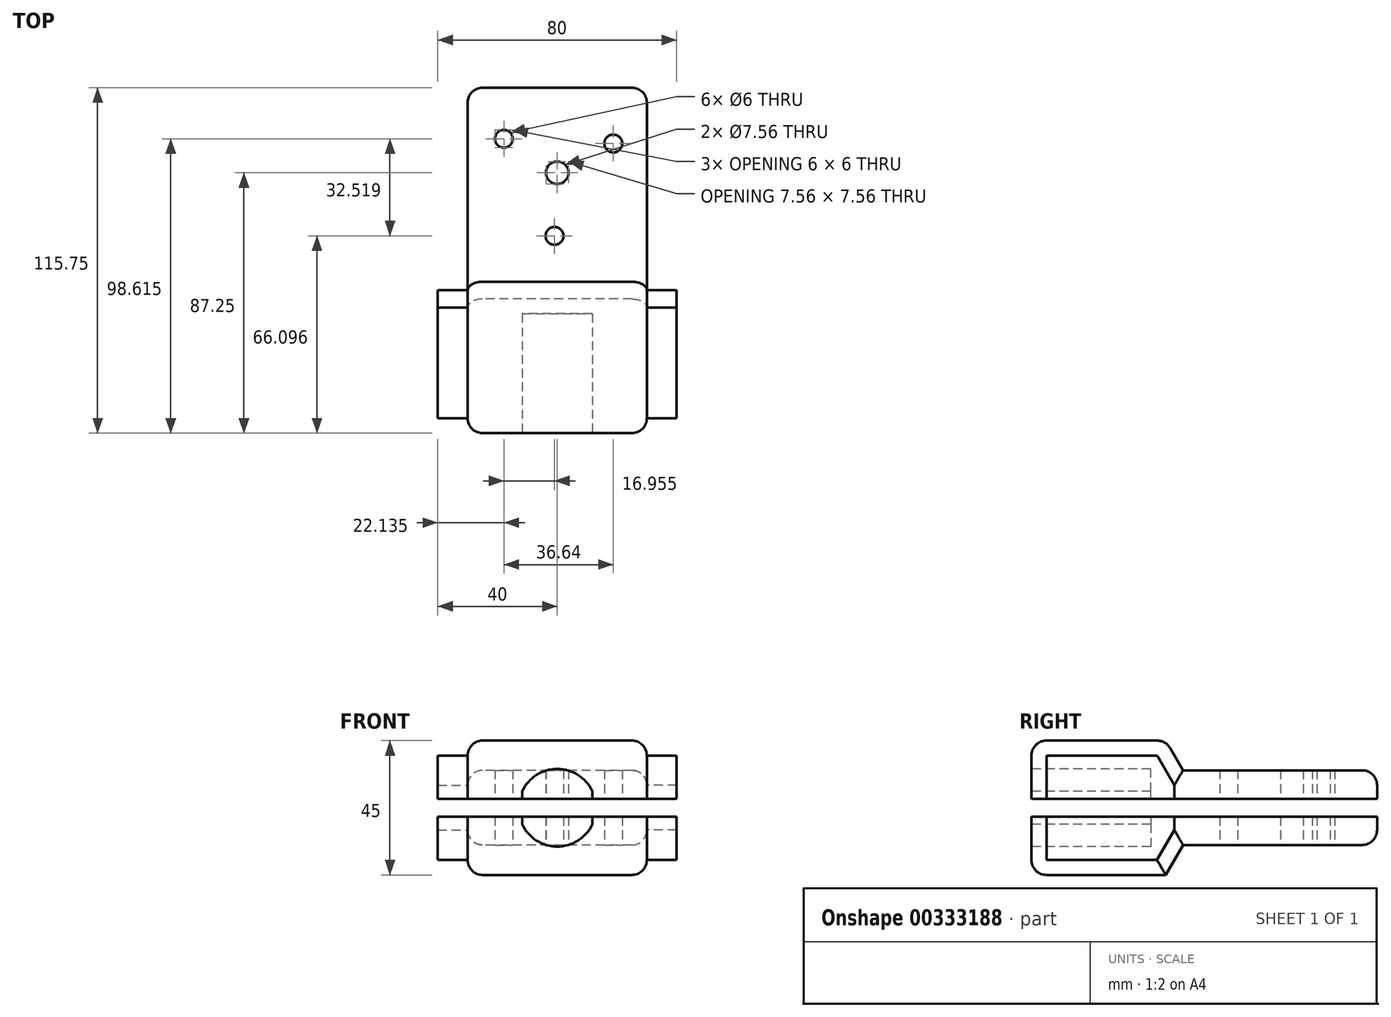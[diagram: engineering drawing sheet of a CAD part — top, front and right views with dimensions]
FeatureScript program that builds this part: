
annotation { "Feature Type Name" : "Feature", "Feature Type Description" : "" }
export const myFeature = defineFeature(function(context is Context, id is Id, definition is map)
    precondition{}
    {
        {
            var Q0;
            Q0=qCreatedBy(makeId("Right.planeOp"),FACE);
            var sketch = newSketch(context, id + "F0", { "sketchPlane" : qUnion([Q0])});
            skLineSegment(sketch, "E0", {"start": v(-50.75, 9.96) * mm, "end": v(-5.75, 9.96) * mm});
            skLineSegment(sketch, "E1", {"start": v(65, 0) * mm, "end": v(65, -25) * mm});
            skLineSegment(sketch, "E2", {"start": v(65, -25) * mm, "end": v(0, -25) * mm});
            skLineSegment(sketch, "E3", {"start": v(0, -25) * mm, "end": v(-5.8, -35.04) * mm});
            skLineSegment(sketch, "E4", {"start": v(-5.8, -35.04) * mm, "end": v(-50.75, -35.04) * mm});
            skLineSegment(sketch, "E5", {"start": v(-50.75, -35.04) * mm, "end": v(-50.75, 9.96) * mm});
            skLineSegment(sketch, "E6", {"start": v(0, 0) * mm, "end": v(-5.75, 9.96) * mm});
            skLineSegment(sketch, "E7", {"start": v(0, 0) * mm, "end": v(65, 0) * mm});
            skSolve(sketch);
        }
        {
            var Q0;
            Q0=qSketchRegion(id+"F0",true);
            extrude(context, id + "F1", {"entities" : qUnion([Q0]), "endBound" : BoundingType.SYMMETRIC, "depth" : 60 * mm});
        }
        {
            var Q0;
            Q0=makeQuery(id+"F1.opExtrude","SWEPT_FACE",FACE,{"disambiguationData":[OSD([sQuery(id+"F0.wireOp",EDGE,"E5")])]});
            var sketch = newSketch(context, id + "F2", { "sketchPlane" : qUnion([Q0])});
            skLineSegment(sketch, "E8", {"start": v(0, -35.04) * mm, "end": v(0, 9.96) * mm, "construction": true});
            skCircle(sketch, "E9", {"center": v(0, -12.54) * mm, "radius": 13 * mm});
            skSolve(sketch);
        }
        {
            var Q0;
            Q0=qSketchRegion(id+"F2",true);
            extrude(context, id + "F3", {"entities" : qUnion([Q0]), "operationType" : NewBodyOperationType.REMOVE, "oppositeDirection" : true, "depth" : 40 * mm});
        }
        {
            var Q0;
            Q0=makeQuery(id+"F1.opExtrude","SWEPT_EDGE",EDGE,{"disambiguationData":[OSD([sQuery(id+"F0.wireOp",EDGE,"E1"),sQuery(id+"F0.wireOp",EDGE,"E7")])]});
            var Q1;
            Q1=makeQuery(id+"F1.opExtrude","SWEPT_EDGE",EDGE,{"disambiguationData":[OSD([sQuery(id+"F0.wireOp",EDGE,"E1"),sQuery(id+"F0.wireOp",EDGE,"E2")])]});
            var Q2;
            Q2=makeQuery(id+"F1.opExtrude","CAP_EDGE",EDGE,{"disambiguationData":[OSD([sQuery(id+"F0.wireOp",EDGE,"E1")])],"isStart":true});
            var Q3;
            Q3=makeQuery(id+"F1.opExtrude","CAP_EDGE",EDGE,{"disambiguationData":[OSD([sQuery(id+"F0.wireOp",EDGE,"E1")])],"isStart":false});
            var Q4;
            Q4=makeQuery(id+"F1.opExtrude","CAP_EDGE",EDGE,{"disambiguationData":[OSD([sQuery(id+"F0.wireOp",EDGE,"E7")])],"isStart":false});
            var Q5;
            Q5=makeQuery(id+"F1.opExtrude","CAP_EDGE",EDGE,{"disambiguationData":[OSD([sQuery(id+"F0.wireOp",EDGE,"E2")])],"isStart":false});
            var Q6;
            Q6=makeQuery(id+"F1.opExtrude","CAP_EDGE",EDGE,{"disambiguationData":[OSD([sQuery(id+"F0.wireOp",EDGE,"E2")])],"isStart":true});
            var Q7;
            Q7=makeQuery(id+"F1.opExtrude","CAP_EDGE",EDGE,{"disambiguationData":[OSD([sQuery(id+"F0.wireOp",EDGE,"E7")])],"isStart":true});
            var Q8;
            Q8=makeQuery(id+"F1.opExtrude","SWEPT_EDGE",EDGE,{"disambiguationData":[OSD([sQuery(id+"F0.wireOp",EDGE,"E0"),sQuery(id+"F0.wireOp",EDGE,"E6")])]});
            var Q9;
            Q9=makeQuery(id+"F1.opExtrude","CAP_EDGE",EDGE,{"disambiguationData":[OSD([sQuery(id+"F0.wireOp",EDGE,"E0")])],"isStart":false});
            var Q10;
            Q10=makeQuery(id+"F1.opExtrude","SWEPT_EDGE",EDGE,{"disambiguationData":[OSD([sQuery(id+"F0.wireOp",EDGE,"E0"),sQuery(id+"F0.wireOp",EDGE,"E5")])]});
            var Q11;
            Q11=makeQuery(id+"F1.opExtrude","CAP_EDGE",EDGE,{"disambiguationData":[OSD([sQuery(id+"F0.wireOp",EDGE,"E0")])],"isStart":true});
            var Q12;
            Q12=makeQuery(id+"F1.opExtrude","CAP_EDGE",EDGE,{"disambiguationData":[OSD([sQuery(id+"F0.wireOp",EDGE,"E6")])],"isStart":false});
            var Q13;
            Q13=makeQuery(id+"F1.opExtrude","CAP_EDGE",EDGE,{"disambiguationData":[OSD([sQuery(id+"F0.wireOp",EDGE,"E6")])],"isStart":true});
            var Q14;
            Q14=makeQuery(id+"F1.opExtrude","CAP_EDGE",EDGE,{"disambiguationData":[OSD([sQuery(id+"F0.wireOp",EDGE,"E3")])],"isStart":false});
            var Q15;
            Q15=makeQuery(id+"F1.opExtrude","CAP_EDGE",EDGE,{"disambiguationData":[OSD([sQuery(id+"F0.wireOp",EDGE,"E3")])],"isStart":true});
            var Q16;
            Q16=makeQuery(id+"F1.opExtrude","CAP_EDGE",EDGE,{"disambiguationData":[OSD([sQuery(id+"F0.wireOp",EDGE,"E4")])],"isStart":false});
            var Q17;
            Q17=makeQuery(id+"F1.opExtrude","CAP_EDGE",EDGE,{"disambiguationData":[OSD([sQuery(id+"F0.wireOp",EDGE,"E4")])],"isStart":true});
            var Q18;
            Q18=makeQuery(id+"F1.opExtrude","SWEPT_EDGE",EDGE,{"disambiguationData":[OSD([sQuery(id+"F0.wireOp",EDGE,"E4"),sQuery(id+"F0.wireOp",EDGE,"E5")])]});
            var Q19;
            Q19=makeQuery(id+"F1.opExtrude","CAP_EDGE",EDGE,{"disambiguationData":[OSD([sQuery(id+"F0.wireOp",EDGE,"E5")])],"isStart":false});
            var Q20;
            Q20=makeQuery(id+"F1.opExtrude","CAP_EDGE",EDGE,{"disambiguationData":[OSD([sQuery(id+"F0.wireOp",EDGE,"E5")])],"isStart":true});
            fillet(context, id + "F4", {"entities" : qUnion([Q0, Q1, Q2, Q3, Q4, Q5, Q6, Q7, Q8, Q9, Q10, Q11, Q12, Q13, Q14, Q15, Q16, Q17, Q18, Q19, Q20]), "radius" : 5 * mm, "tangentPropagation" : true, "allowEdgeOverflow" : false});
        }
        {
            var Q0;
            Q0=makeQuery(id+"F1.opExtrude","SWEPT_FACE",FACE,{"disambiguationData":[OSD([sQuery(id+"F0.wireOp",EDGE,"E2")])]});
            var sketch = newSketch(context, id + "F5", { "sketchPlane" : qUnion([Q0])});
            skCircle(sketch, "E10", {"center": v(-17.86, -47.86) * mm, "radius": 3 * mm});
            skCircle(sketch, "E11.1.0", {"center": v(18.77, -46.29) * mm, "radius": 3 * mm});
            skCircle(sketch, "E11.2.0", {"center": v(-0.9, -15.35) * mm, "radius": 3 * mm});
            skPoint(sketch, "E11.center", {"position": v(0, -36.5) * mm});
            skCircle(sketch, "E12", {"center": v(0, -36.5) * mm, "radius": 3.78 * mm});
            skSolve(sketch);
        }
        {
            var Q0;
            Q0=qSketchRegion(id+"F5",true);
            extrude(context, id + "F6", {"entities" : qUnion([Q0]), "operationType" : NewBodyOperationType.REMOVE, "oppositeDirection" : true, "depth" : 39.9 * mm});
        }
        {
            var Q0;
            Q0=makeQuery(id+"F1.opExtrude","SWEPT_FACE",FACE,{"disambiguationData":[OSD([sQuery(id+"F0.wireOp",EDGE,"E5")])]});
            var sketch = newSketch(context, id + "F7", { "sketchPlane" : qUnion([Q0])});
            skLineSegment(sketch, "E13", {"start": v(-25, -7.04) * mm, "end": v(25, -7.04) * mm});
            skLineSegment(sketch, "E14", {"start": v(25, -7.04) * mm, "end": v(25, -18.04) * mm});
            skLineSegment(sketch, "E15", {"start": v(25, -18.04) * mm, "end": v(-25, -18.04) * mm});
            skLineSegment(sketch, "E16", {"start": v(-25, -18.04) * mm, "end": v(-25, -7.04) * mm});
            skLineSegment(sketch, "E17", {"start": v(-25, -7.04) * mm, "end": v(-35.45, -7.04) * mm});
            skLineSegment(sketch, "E18", {"start": v(-35.45, -7.04) * mm, "end": v(-35.45, -18.04) * mm});
            skLineSegment(sketch, "E19", {"start": v(-35.45, -18.04) * mm, "end": v(-25, -18.04) * mm});
            skLineSegment(sketch, "E20", {"start": v(25, -7.04) * mm, "end": v(35.45, -7.04) * mm});
            skLineSegment(sketch, "E21", {"start": v(35.45, -7.04) * mm, "end": v(35.45, -18.04) * mm});
            skLineSegment(sketch, "E22", {"start": v(35.45, -18.04) * mm, "end": v(25, -18.04) * mm});
            skSolve(sketch);
        }
        {
            var Q0;
            Q0=qSketchRegion(id+"F7",true);
            extrude(context, id + "F8", {"entities" : qUnion([Q0]), "operationType" : NewBodyOperationType.REMOVE, "oppositeDirection" : true, "depth" : 159.3 * mm});
        }
        {
            var Q0;
            Q0=makeQuery(id+"F1.opExtrude","CAP_FACE",FACE,{"disambiguationData":[OSD([sQuery(id+"F0.wireOp",EDGE,"E0"),sQuery(id+"F0.wireOp",EDGE,"E1"),sQuery(id+"F0.wireOp",EDGE,"E2"),sQuery(id+"F0.wireOp",EDGE,"E3"),sQuery(id+"F0.wireOp",EDGE,"E4"),sQuery(id+"F0.wireOp",EDGE,"E5"),sQuery(id+"F0.wireOp",EDGE,"E6"),sQuery(id+"F0.wireOp",EDGE,"E7")])],"isStart":false});
            extrude(context, id + "F9", {"entities" : qUnion([Q0]), "operationType" : NewBodyOperationType.ADD, "depth" : 10 * mm});
        }
        {
            var Q0;
            {var subQ0=sQuery(id+"F0.wireOp",EDGE,"E7");var subQ1=sQuery(id+"F0.wireOp",EDGE,"E6");var subQ2=sQuery(id+"F0.wireOp",EDGE,"E5");var subQ3=sQuery(id+"F0.wireOp",EDGE,"E4");var subQ4=sQuery(id+"F0.wireOp",EDGE,"E3");var subQ5=sQuery(id+"F0.wireOp",EDGE,"E2");var subQ6=sQuery(id+"F0.wireOp",EDGE,"E1");var subQ7=sQuery(id+"F0.wireOp",EDGE,"E0");Q0=makeQuery(id+"F9.opExtrude","SWEPT_FACE",FACE,{"disambiguationData":[OSD([subQ7,subQ6,subQ5,subQ4,subQ3,subQ2,subQ1,subQ0]),TDD([makeQuery(id+"F4.opFillet","BLEND_EDGE",EDGE,{"blendedFrom":[makeQuery(id+"F1.opExtrude","CAP_EDGE",EDGE,{"disambiguationData":[OSD([subQ0])],"isStart":false}),makeQuery(id+"F1.opExtrude","CAP_FACE",FACE,{"disambiguationData":[OSD([subQ7,subQ6,subQ5,subQ4,subQ3,subQ2,subQ1,subQ0])],"isStart":false})],"blendedInto":[makeQuery(id+"F1.opExtrude","CAP_FACE",FACE,{"disambiguationData":[OSD([subQ7,subQ6,subQ5,subQ4,subQ3,subQ2,subQ1,subQ0])],"isStart":false})]})])]});}
            extrude(context, id + "F10", {"entities" : qUnion([Q0]), "operationType" : NewBodyOperationType.REMOVE, "oppositeDirection" : true, "depth" : 25 * mm});
        }
        {
            var Q0;
            Q0=makeQuery(id+"F1.opExtrude","CAP_FACE",FACE,{"disambiguationData":[OSD([sQuery(id+"F0.wireOp",EDGE,"E0"),sQuery(id+"F0.wireOp",EDGE,"E1"),sQuery(id+"F0.wireOp",EDGE,"E2"),sQuery(id+"F0.wireOp",EDGE,"E3"),sQuery(id+"F0.wireOp",EDGE,"E4"),sQuery(id+"F0.wireOp",EDGE,"E5"),sQuery(id+"F0.wireOp",EDGE,"E6"),sQuery(id+"F0.wireOp",EDGE,"E7")])],"isStart":true});
            extrude(context, id + "F11", {"entities" : qUnion([Q0]), "operationType" : NewBodyOperationType.ADD, "depth" : 10 * mm});
        }
        {
            var Q0;
            {var subQ0=sQuery(id+"F0.wireOp",EDGE,"E7");var subQ1=sQuery(id+"F0.wireOp",EDGE,"E6");var subQ2=sQuery(id+"F0.wireOp",EDGE,"E5");var subQ3=sQuery(id+"F0.wireOp",EDGE,"E4");var subQ4=sQuery(id+"F0.wireOp",EDGE,"E3");var subQ5=sQuery(id+"F0.wireOp",EDGE,"E2");var subQ6=sQuery(id+"F0.wireOp",EDGE,"E1");var subQ7=sQuery(id+"F0.wireOp",EDGE,"E0");Q0=makeQuery(id+"F11.opExtrude","SWEPT_FACE",FACE,{"disambiguationData":[OSD([subQ7,subQ6,subQ5,subQ4,subQ3,subQ2,subQ1,subQ0]),TDD([makeQuery(id+"F4.opFillet","BLEND_EDGE",EDGE,{"blendedFrom":[makeQuery(id+"F1.opExtrude","CAP_EDGE",EDGE,{"disambiguationData":[OSD([subQ0])],"isStart":true}),makeQuery(id+"F1.opExtrude","CAP_FACE",FACE,{"disambiguationData":[OSD([subQ7,subQ6,subQ5,subQ4,subQ3,subQ2,subQ1,subQ0])],"isStart":true})],"blendedInto":[makeQuery(id+"F1.opExtrude","CAP_FACE",FACE,{"disambiguationData":[OSD([subQ7,subQ6,subQ5,subQ4,subQ3,subQ2,subQ1,subQ0])],"isStart":true})]})])]});}
            extrude(context, id + "F12", {"entities" : qUnion([Q0]), "operationType" : NewBodyOperationType.REMOVE, "oppositeDirection" : true, "depth" : 25 * mm});
        }
        {
            var Q0;
            {var subQ0=sQuery(id+"F7.wireOp",EDGE,"E20");var subQ1=sQuery(id+"F7.wireOp",EDGE,"E17");var subQ2=sQuery(id+"F7.wireOp",EDGE,"E13");var subQ3=sQuery(id+"F0.wireOp",EDGE,"E7");var subQ4=sQuery(id+"F0.wireOp",EDGE,"E6");var subQ5=sQuery(id+"F0.wireOp",EDGE,"E5");var subQ6=sQuery(id+"F0.wireOp",EDGE,"E4");var subQ7=sQuery(id+"F0.wireOp",EDGE,"E3");var subQ8=sQuery(id+"F0.wireOp",EDGE,"E2");var subQ9=sQuery(id+"F0.wireOp",EDGE,"E1");var subQ10=sQuery(id+"F0.wireOp",EDGE,"E0");Q0=makeQuery(id+"F11.boolean.opBoolean","MERGE",FACE,{"derivedFrom":[makeQuery(id+"F9.boolean.opBoolean","MERGE",FACE,{"derivedFrom":[makeQuery(id+"F8.boolean.opBoolean","COPY",FACE,{"derivedFrom":makeQuery(id+"F8.opExtrude","SWEPT_FACE",FACE,{"disambiguationData":[OSD([subQ2,subQ1,subQ0])]})}),makeQuery(id+"F9.opExtrude","SWEPT_FACE",FACE,{"disambiguationData":[OSD([subQ10,subQ9,subQ8,subQ7,subQ6,subQ5,subQ4,subQ3,subQ2,subQ1,subQ0])]})]}),makeQuery(id+"F11.opExtrude","SWEPT_FACE",FACE,{"disambiguationData":[OSD([subQ10,subQ9,subQ8,subQ7,subQ6,subQ5,subQ4,subQ3,subQ2,subQ1,subQ0])]})]});}
            extrude(context, id + "F13", {"entities" : qUnion([Q0]), "operationType" : NewBodyOperationType.ADD, "depth" : 2.5 * mm});
        }
        {
            var Q0;
            {var subQ0=sQuery(id+"F7.wireOp",EDGE,"E22");var subQ1=sQuery(id+"F7.wireOp",EDGE,"E19");var subQ2=sQuery(id+"F7.wireOp",EDGE,"E15");var subQ3=sQuery(id+"F0.wireOp",EDGE,"E7");var subQ4=sQuery(id+"F0.wireOp",EDGE,"E6");var subQ5=sQuery(id+"F0.wireOp",EDGE,"E5");var subQ6=sQuery(id+"F0.wireOp",EDGE,"E4");var subQ7=sQuery(id+"F0.wireOp",EDGE,"E3");var subQ8=sQuery(id+"F0.wireOp",EDGE,"E2");var subQ9=sQuery(id+"F0.wireOp",EDGE,"E1");var subQ10=sQuery(id+"F0.wireOp",EDGE,"E0");Q0=makeQuery(id+"F11.boolean.opBoolean","MERGE",FACE,{"derivedFrom":[makeQuery(id+"F9.boolean.opBoolean","MERGE",FACE,{"derivedFrom":[makeQuery(id+"F8.boolean.opBoolean","COPY",FACE,{"derivedFrom":makeQuery(id+"F8.opExtrude","SWEPT_FACE",FACE,{"disambiguationData":[OSD([subQ2,subQ1,subQ0])]})}),makeQuery(id+"F9.opExtrude","SWEPT_FACE",FACE,{"disambiguationData":[OSD([subQ10,subQ9,subQ8,subQ7,subQ6,subQ5,subQ4,subQ3,subQ2,subQ1,subQ0])]})]}),makeQuery(id+"F11.opExtrude","SWEPT_FACE",FACE,{"disambiguationData":[OSD([subQ10,subQ9,subQ8,subQ7,subQ6,subQ5,subQ4,subQ3,subQ2,subQ1,subQ0])]})]});}
            extrude(context, id + "F14", {"entities" : qUnion([Q0]), "operationType" : NewBodyOperationType.ADD, "depth" : 2.5 * mm});
        }
    });
